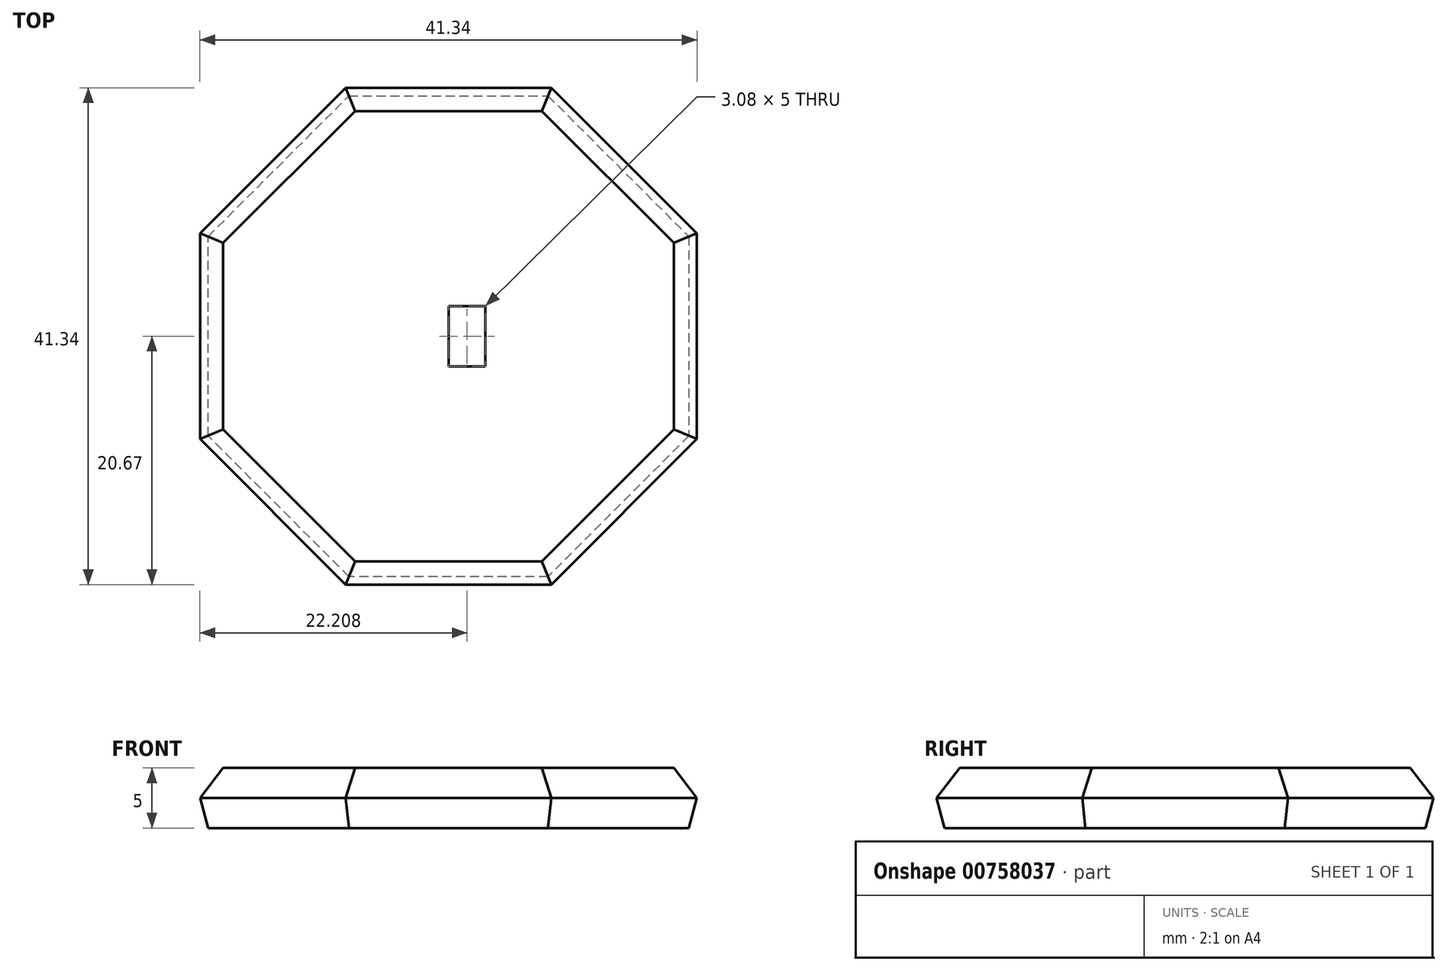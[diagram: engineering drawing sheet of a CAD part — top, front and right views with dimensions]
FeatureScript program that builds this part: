
annotation { "Feature Type Name" : "Feature", "Feature Type Description" : "" }
export const myFeature = defineFeature(function(context is Context, id is Id, definition is map)
    precondition{}
    {
        {
            var Q0;
            Q0=qCreatedBy(makeId("Top.planeOp"),FACE);
            var sketch = newSketch(context, id + "F0", { "sketchPlane" : qUnion([Q0])});
            skCircle(sketch, "E0.cCircle", {"center": v(0, 0) * mm, "radius": 20 * mm, "construction": true});
            skLineSegment(sketch, "E0.0", {"start": v(-20, -8.28) * mm, "end": v(-20, 8.28) * mm});
            skLineSegment(sketch, "E0.1", {"start": v(-20, 8.28) * mm, "end": v(-8.28, 20) * mm});
            skLineSegment(sketch, "E0.2", {"start": v(-8.28, 20) * mm, "end": v(8.28, 20) * mm});
            skLineSegment(sketch, "E0.3", {"start": v(8.28, 20) * mm, "end": v(20, 8.28) * mm});
            skLineSegment(sketch, "E0.4", {"start": v(20, 8.28) * mm, "end": v(20, -8.28) * mm});
            skLineSegment(sketch, "E0.5", {"start": v(20, -8.28) * mm, "end": v(8.28, -20) * mm});
            skLineSegment(sketch, "E0.6", {"start": v(8.28, -20) * mm, "end": v(-8.28, -20) * mm});
            skLineSegment(sketch, "E0.7", {"start": v(-8.28, -20) * mm, "end": v(-20, -8.28) * mm});
            skPoint(sketch, "E0.0.midPoint", {"position": v(-20, 0) * mm});
            skSolve(sketch);
        }
        {
            var Q0;
            Q0 = qSketchRegion(id + "F0", true);
            extrude(context, id + "F1", {"entities" : qUnion([Q0]), "depth" : 5 * mm, "offsetDistance" : 25 * mm, "hasDraft" : true, "draftAngle" : 15 * degree});
        }
        {
            var Q0;
            Q0=makeQuery(id+"F1.opExtrude","CAP_EDGE",EDGE,{"disambiguationData":[OSD([sQuery(id+"F0.wireOp",EDGE,"E0.7")])],"isStart":false});
            var Q1;
            Q1=makeQuery(id+"F1.opExtrude","CAP_EDGE",EDGE,{"disambiguationData":[OSD([sQuery(id+"F0.wireOp",EDGE,"E0.6")])],"isStart":false});
            var Q2;
            Q2=makeQuery(id+"F1.opExtrude","CAP_EDGE",EDGE,{"disambiguationData":[OSD([sQuery(id+"F0.wireOp",EDGE,"E0.5")])],"isStart":false});
            var Q3;
            Q3=makeQuery(id+"F1.opExtrude","CAP_EDGE",EDGE,{"disambiguationData":[OSD([sQuery(id+"F0.wireOp",EDGE,"E0.0")])],"isStart":false});
            var Q4;
            Q4=makeQuery(id+"F1.opExtrude","CAP_EDGE",EDGE,{"disambiguationData":[OSD([sQuery(id+"F0.wireOp",EDGE,"E0.1")])],"isStart":false});
            var Q5;
            Q5=makeQuery(id+"F1.opExtrude","CAP_FACE",FACE,{"disambiguationData":[OSD([sQuery(id+"F0.wireOp",EDGE,"E0.0"),sQuery(id+"F0.wireOp",EDGE,"E0.1"),sQuery(id+"F0.wireOp",EDGE,"E0.2"),sQuery(id+"F0.wireOp",EDGE,"E0.3"),sQuery(id+"F0.wireOp",EDGE,"E0.4"),sQuery(id+"F0.wireOp",EDGE,"E0.5"),sQuery(id+"F0.wireOp",EDGE,"E0.6"),sQuery(id+"F0.wireOp",EDGE,"E0.7")])],"isStart":false});
            chamfer(context, id + "F2", {"entities" : qUnion([Q0, Q1, Q2, Q3, Q4, Q5]), "width" : 2 * mm, "tangentPropagation" : true});
        }
        {
            var Q0;
            Q0=makeQuery(id+"F1.opExtrude","CAP_FACE",FACE,{"disambiguationData":[OSD([sQuery(id+"F0.wireOp",EDGE,"E0.0"),sQuery(id+"F0.wireOp",EDGE,"E0.1"),sQuery(id+"F0.wireOp",EDGE,"E0.2"),sQuery(id+"F0.wireOp",EDGE,"E0.3"),sQuery(id+"F0.wireOp",EDGE,"E0.4"),sQuery(id+"F0.wireOp",EDGE,"E0.5"),sQuery(id+"F0.wireOp",EDGE,"E0.6"),sQuery(id+"F0.wireOp",EDGE,"E0.7")])],"isStart":false});
            var sketch = newSketch(context, id + "F3", { "sketchPlane" : qUnion([Q0])});
            skLineSegment(sketch, "E1.bottom", {"start": v(0, 2.5) * mm, "end": v(3.07, 2.5) * mm});
            skLineSegment(sketch, "E1.top", {"start": v(0, -2.5) * mm, "end": v(3.07, -2.5) * mm});
            skLineSegment(sketch, "E1.left", {"start": v(0, 2.5) * mm, "end": v(0, -2.5) * mm});
            skLineSegment(sketch, "E1.right", {"start": v(3.08, 2.5) * mm, "end": v(3.07, -2.5) * mm});
            skSolve(sketch);
        }
        {
            var Q0;
            Q0=makeQuery(id+"F3.imprint","IMPRINT",FACE,{"disambiguationData":[TD([[makeQuery(id+"F3.imprint","IMPRINT",EDGE,{"derivedFrom":sQuery(id+"F3.wireOp",EDGE,"E1.bottom")}),-1.0]])]});
            extrude(context, id + "F4", {"entities" : qUnion([Q0]), "operationType" : NewBodyOperationType.REMOVE, "oppositeDirection" : true, "depth" : 5 * mm, "offsetDistance" : 25 * mm});
        }
    });
